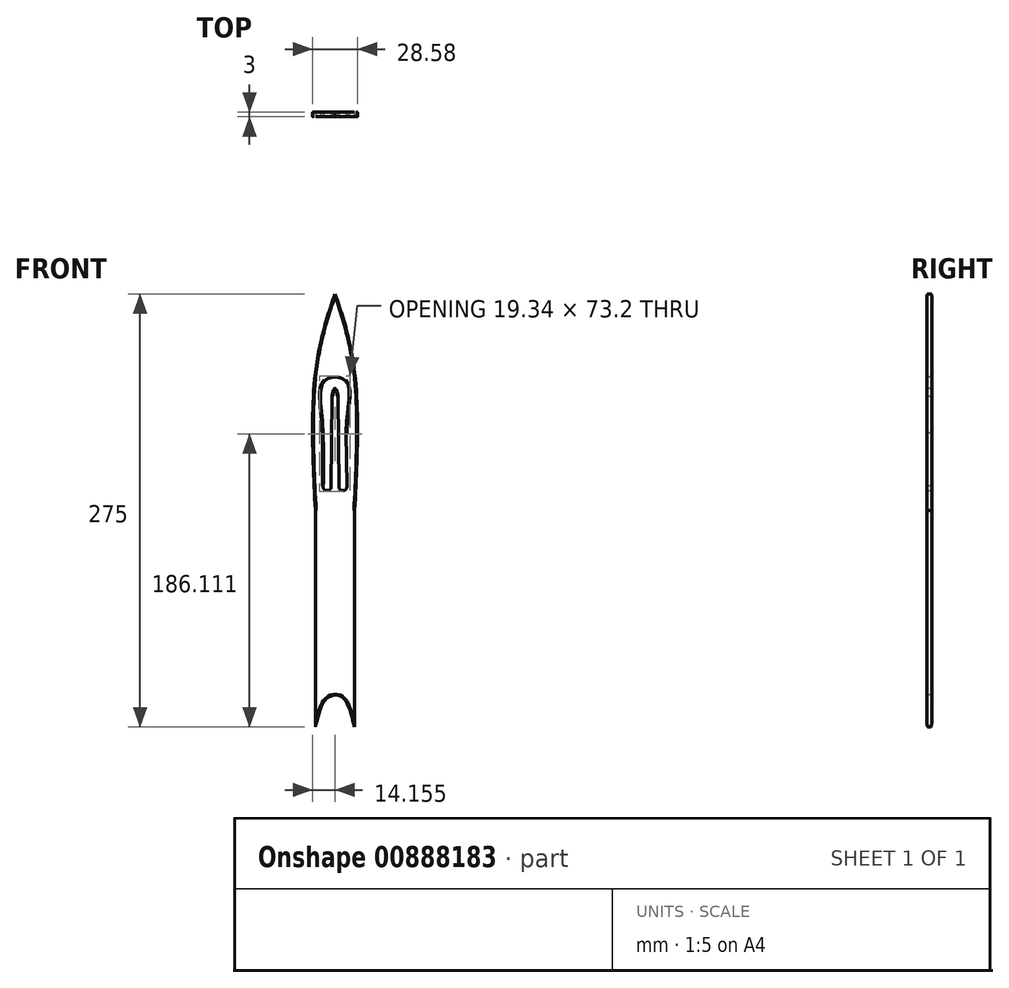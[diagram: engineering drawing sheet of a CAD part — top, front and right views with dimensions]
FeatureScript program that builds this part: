
annotation { "Feature Type Name" : "Feature", "Feature Type Description" : "" }
export const myFeature = defineFeature(function(context is Context, id is Id, definition is map)
    precondition{}
    {
        {
            var Q0;
            Q0=qCreatedBy(makeId("Front.planeOp"),FACE);
            var sketch = newSketch(context, id + "F0", { "sketchPlane" : qUnion([Q0])});
            skLineSegment(sketch, "E0.left", {"start": v(12.5, 87.5) * mm, "end": v(12.5, -137.5) * mm});
            skLineSegment(sketch, "E0.right", {"start": v(-12.5, 87.5) * mm, "end": v(-12.5, -137.5) * mm});
            skPoint(sketch, "E0.middle", {"position": v(0, 0) * mm});
            skFitSpline(sketch, "E1", {"points": [v(12.5, 0) * mm, v(12.5, 87.5) * mm, v(0, 137.5) * mm], "startDerivative": vector(8.6, 170.74) * mm, "endDerivative": vector(-35.94, 100.57) * mm});
            skFitSpline(sketch, "E2.MirrorCS", {"points": [v(-12.5, 0) * mm, v(-12.5, 87.5) * mm, v(0, 137.5) * mm], "startDerivative": vector(-8.6, 170.74) * mm, "endDerivative": vector(35.94, 100.57) * mm});
            skPoint(sketch, "E3.orphan", {"position": v(-12.5, 137.5) * mm});
            skPoint(sketch, "E4.orphan", {"position": v(12.5, 137.5) * mm});
            skFitSpline(sketch, "E5", {"points": [v(-12.5, -137.5) * mm, v(-5.5, -119.5) * mm, v(5.5, -119.5) * mm, v(12.5, -137.5) * mm], "startDerivative": vector(11.21, 39.37) * mm, "endDerivative": vector(14.5, -40.92) * mm});
            skFitSpline(sketch, "E6", {"points": [v(-7.5, 12.5) * mm, v(-8.32, 59.7) * mm, v(-6.5, 82.5) * mm, v(6.5, 82.5) * mm, v(7.75, 60.25) * mm, v(7.5, 12.5) * mm], "startDerivative": vector(3, 214.4) * mm, "endDerivative": vector(9.26, -213.97) * mm});
            skLineSegment(sketch, "E7", {"start": v(6.5, 82.5) * mm, "end": v(7.47, 14.61) * mm});
            skLineSegment(sketch, "E8", {"start": v(-6.5, 82.5) * mm, "end": v(-7.47, 14.61) * mm});
            skArc(sketch, "E9", {"start": v(-7.46, 15.46) * mm, "mid": v(-5.23, 12.51) * mm, "end": v(-2.5, 15) * mm});
            skArc(sketch, "E10", {"start": v(2.5, 15) * mm, "mid": v(5.23, 12.51) * mm, "end": v(7.46, 15.46) * mm});
            skFitSpline(sketch, "E11.trimOffspring", {"points": [v(2.5, 12.5) * mm, v(2, 72.5) * mm, v(0, 77.5) * mm, v(-2, 72.5) * mm, v(-2.5, 12.5) * mm], "startDerivative": vector(7.14, 215.08) * mm, "endDerivative": vector(2.46, -212.67) * mm});
            skLineSegment(sketch, "E12", {"start": v(-2, 72.5) * mm, "end": v(-2.5, 15) * mm});
            skLineSegment(sketch, "E13", {"start": v(2, 72.5) * mm, "end": v(2.5, 15) * mm});
            skSolve(sketch);
        }
        {
            var Q0;
            Q0 = qSketchRegion(id + "F0", true);
            extrude(context, id + "F1", {"entities" : qUnion([Q0]), "oppositeDirection" : true, "depth" : 3 * mm, "offsetDistance" : 25 * mm});
        }
        {
            var Q0;
            Q0=makeQuery(id+"F1.opExtrude","CAP_EDGE",EDGE,{"disambiguationData":[OSD([sQuery(id+"F0.wireOp",EDGE,"E1")])],"isStart":true});
            var Q1;
            Q1=makeQuery(id+"F1.opExtrude","CAP_EDGE",EDGE,{"disambiguationData":[OSD([sQuery(id+"F0.wireOp",EDGE,"E1")])],"isStart":false});
            var Q2;
            Q2=makeQuery(id+"F1.opExtrude","CAP_EDGE",EDGE,{"disambiguationData":[OSD([sQuery(id+"F0.wireOp",EDGE,"E0.left")])],"isStart":true});
            var Q3;
            Q3=makeQuery(id+"F1.opExtrude","CAP_EDGE",EDGE,{"disambiguationData":[OSD([sQuery(id+"F0.wireOp",EDGE,"E0.left")])],"isStart":false});
            var Q4;
            Q4=makeQuery(id+"F1.opExtrude","CAP_EDGE",EDGE,{"disambiguationData":[OSD([sQuery(id+"F0.wireOp",EDGE,"E11.trimOffspring")])],"isStart":true});
            var Q5;
            Q5=makeQuery(id+"F1.opExtrude","CAP_EDGE",EDGE,{"disambiguationData":[OSD([sQuery(id+"F0.wireOp",EDGE,"E11.trimOffspring")])],"isStart":false});
            var Q6;
            Q6=makeQuery(id+"F1.opExtrude","CAP_EDGE",EDGE,{"disambiguationData":[OSD([sQuery(id+"F0.wireOp",EDGE,"E13")])],"isStart":true});
            var Q7;
            Q7=makeQuery(id+"F1.opExtrude","CAP_EDGE",EDGE,{"disambiguationData":[OSD([sQuery(id+"F0.wireOp",EDGE,"E13")])],"isStart":false});
            var Q8;
            Q8=makeQuery(id+"F1.opExtrude","CAP_EDGE",EDGE,{"disambiguationData":[OSD([sQuery(id+"F0.wireOp",EDGE,"E2.MirrorCS")])],"isStart":true});
            var Q9;
            Q9=makeQuery(id+"F1.opExtrude","CAP_EDGE",EDGE,{"disambiguationData":[OSD([sQuery(id+"F0.wireOp",EDGE,"E2.MirrorCS")])],"isStart":false});
            var Q10;
            Q10=makeQuery(id+"F1.opExtrude","CAP_EDGE",EDGE,{"disambiguationData":[OSD([sQuery(id+"F0.wireOp",EDGE,"E0.right")])],"isStart":true});
            var Q11;
            Q11=makeQuery(id+"F1.opExtrude","CAP_EDGE",EDGE,{"disambiguationData":[OSD([sQuery(id+"F0.wireOp",EDGE,"E0.right")])],"isStart":false});
            var Q12;
            Q12=makeQuery(id+"F1.opExtrude","CAP_EDGE",EDGE,{"disambiguationData":[OSD([sQuery(id+"F0.wireOp",EDGE,"E12")])],"isStart":false});
            var Q13;
            Q13=makeQuery(id+"F1.opExtrude","CAP_EDGE",EDGE,{"disambiguationData":[OSD([sQuery(id+"F0.wireOp",EDGE,"E12")])],"isStart":true});
            var Q14;
            Q14=makeQuery(id+"F1.opExtrude","CAP_EDGE",EDGE,{"disambiguationData":[OSD([sQuery(id+"F0.wireOp",EDGE,"E7")])],"isStart":false});
            var Q15;
            Q15=makeQuery(id+"F1.opExtrude","CAP_EDGE",EDGE,{"disambiguationData":[OSD([sQuery(id+"F0.wireOp",EDGE,"E7")])],"isStart":true});
            var Q16;
            Q16=makeQuery(id+"F1.opExtrude","CAP_EDGE",EDGE,{"disambiguationData":[OSD([sQuery(id+"F0.wireOp",EDGE,"E6")])],"isStart":true});
            var Q17;
            Q17=makeQuery(id+"F1.opExtrude","CAP_EDGE",EDGE,{"disambiguationData":[OSD([sQuery(id+"F0.wireOp",EDGE,"E6")])],"isStart":false});
            var Q18;
            Q18=makeQuery(id+"F1.opExtrude","CAP_EDGE",EDGE,{"disambiguationData":[OSD([sQuery(id+"F0.wireOp",EDGE,"E8")])],"isStart":true});
            var Q19;
            Q19=makeQuery(id+"F1.opExtrude","CAP_EDGE",EDGE,{"disambiguationData":[OSD([sQuery(id+"F0.wireOp",EDGE,"E8")])],"isStart":false});
            var Q20;
            Q20=makeQuery(id+"F1.opExtrude","CAP_EDGE",EDGE,{"disambiguationData":[OSD([sQuery(id+"F0.wireOp",EDGE,"E5")])],"isStart":true});
            var Q21;
            Q21=makeQuery(id+"F1.opExtrude","CAP_EDGE",EDGE,{"disambiguationData":[OSD([sQuery(id+"F0.wireOp",EDGE,"E5")])],"isStart":false});
            var Q22;
            Q22=makeQuery(id+"F1.opExtrude","CAP_EDGE",EDGE,{"disambiguationData":[OSD([sQuery(id+"F0.wireOp",EDGE,"E10")])],"isStart":false});
            var Q23;
            Q23=makeQuery(id+"F1.opExtrude","CAP_EDGE",EDGE,{"disambiguationData":[OSD([sQuery(id+"F0.wireOp",EDGE,"E10")])],"isStart":true});
            var Q24;
            Q24=makeQuery(id+"F1.opExtrude","CAP_EDGE",EDGE,{"disambiguationData":[OSD([sQuery(id+"F0.wireOp",EDGE,"E9")])],"isStart":false});
            var Q25;
            Q25=makeQuery(id+"F1.opExtrude","CAP_EDGE",EDGE,{"disambiguationData":[OSD([sQuery(id+"F0.wireOp",EDGE,"E9")])],"isStart":true});
            fillet(context, id + "F2", {"entities" : qUnion([Q0, Q1, Q2, Q3, Q4, Q5, Q6, Q7, Q8, Q9, Q10, Q11, Q12, Q13, Q14, Q15, Q16, Q17, Q18, Q19, Q20, Q21, Q22, Q23, Q24, Q25]), "radius" : .5 * mm, "tangentPropagation" : true, "allowEdgeOverflow" : false});
        }
    });
